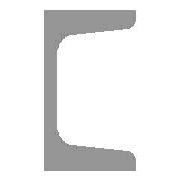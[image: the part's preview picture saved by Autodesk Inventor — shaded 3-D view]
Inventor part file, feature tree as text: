
AUTODESK INVENTOR PART (.ipt)
format: ipt  version: 2023 (Build 270158000, 158)  size: 148,480 bytes
history: native  units: mm (DEFAULTED — no unit token found)
features: other x6, sketch x3, reference x3, hole x1, plane x1
ambient origin geometry x8: Origin, YZ Plane, XZ Plane, XY Plane, X Axis, Y Axis, Z Axis, Center Point
bodies: Solid1 (feature_tree), Body (feature_tree)
feature tree (14):
  other  "Driven Length"
  other  "Start plane"
  other  "End plane"
  hole  "Hole1"  [1 undecoded]
  sketch  "Sketch3"  dims[d0=3.3528mm d1=38.1mm]
  plane  "Work Plane3"
  sketch  "Sketch4"  dims[d2=34.798mm]
  sketch  "Sketch5"  dims[d3=6.9342mm d4=15.650845mm d5=0.820104mm d6=1828.8mm d7=0.0mm d25=0.0mm d26=-0.0mm d27=1828.8mm d28=6.032225mm d29=2.032mm d30=90.0deg d31=1828.8mm d32=6.35mm d33=19.05mm d34=9.525mm d35=6.35mm d36=14.3117mm d37=25.4mm d38=20.594885mm]
  reference  "Reference1"
  reference  "Reference2"
  reference  "Reference3"
  other  "<userpath>\Documents\AVA\202207 Model States\Support Structure.iam"
  other  "Support Structure.iam"
  other  "Flexible Bracket:1"
note: 1 required parameter value undecoded (feature->parameter linkage not recoverable at this tier; creation-order binding heuristic only, values carry confidence <= 0.55)
